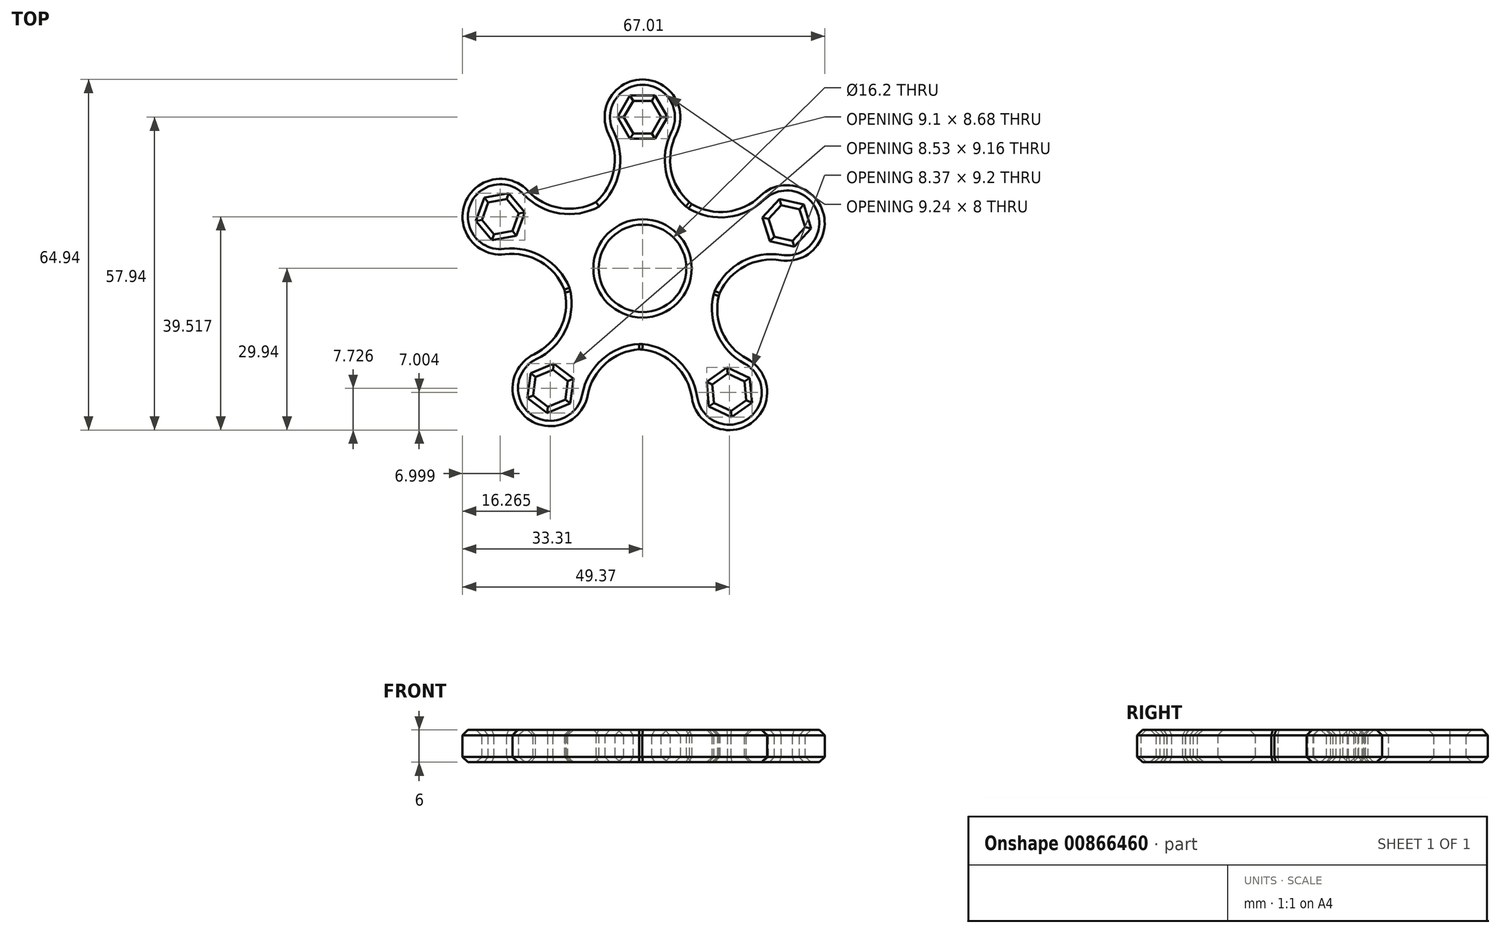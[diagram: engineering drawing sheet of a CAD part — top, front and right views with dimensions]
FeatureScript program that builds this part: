
annotation { "Feature Type Name" : "Feature", "Feature Type Description" : "" }
export const myFeature = defineFeature(function(context is Context, id is Id, definition is map)
    precondition{}
    {
        {
            var Q0;
            Q0=qCreatedBy(makeId("Top.planeOp"),FACE);
            var sketch = newSketch(context, id + "F0", { "sketchPlane" : qUnion([Q0])});
            skCircle(sketch, "E0", {"center": v(0, 0) * mm, "radius": 35 * mm, "construction": true});
            skCircle(sketch, "E1", {"center": v(0, 0) * mm, "radius": 8.1 * mm});
            skCircle(sketch, "E2", {"center": v(0, 0) * mm, "radius": 15 * mm});
            skLineSegment(sketch, "E3", {"start": v(0, 0) * mm, "end": v(0, 35) * mm, "construction": true});
            skLineSegment(sketch, "E4.1.0", {"start": v(0, 0) * mm, "end": v(33.38, 10.52) * mm, "construction": true});
            skLineSegment(sketch, "E4.2.0", {"start": v(0, 0) * mm, "end": v(20.08, -28.67) * mm, "construction": true});
            skLineSegment(sketch, "E4.3.0", {"start": v(0, 0) * mm, "end": v(-21.3, -27.77) * mm, "construction": true});
            skLineSegment(sketch, "E4.4.0", {"start": v(0, 0) * mm, "end": v(-32.89, 11.97) * mm, "construction": true});
            skLineSegment(sketch, "E4.anchor2", {"start": v(0, 0) * mm, "end": v(-32.89, 11.97) * mm, "construction": true});
            skCircle(sketch, "E5", {"center": v(0, 28) * mm, "radius": 7 * mm});
            skArc(sketch, "E6", {"start": v(-8.63, 12.27) * mm, "mid": v(-5.3, 18.15) * mm, "end": v(-6.25, 24.84) * mm});
            skArc(sketch, "E7.MirrorCS", {"start": v(8.63, 12.27) * mm, "mid": v(5.3, 18.15) * mm, "end": v(6.25, 24.84) * mm});
            skArc(sketch, "E8.1.1", {"start": v(14.3, -4.55) * mm, "mid": v(18.9, 0.4) * mm, "end": v(25.57, 1.51) * mm});
            skCircle(sketch, "E8.1.2", {"center": v(26.7, 8.42) * mm, "radius": 7 * mm});
            skArc(sketch, "E8.1.3", {"start": v(9.1, 11.92) * mm, "mid": v(15.71, 10.51) * mm, "end": v(21.81, 13.43) * mm});
            skArc(sketch, "E8.2.1", {"start": v(-0.04, -15) * mm, "mid": v(6.07, -17.9) * mm, "end": v(9.13, -23.93) * mm});
            skCircle(sketch, "E8.2.2", {"center": v(16.06, -22.94) * mm, "radius": 7 * mm});
            skArc(sketch, "E8.2.3", {"start": v(14.1, -5.1) * mm, "mid": v(14.75, -11.82) * mm, "end": v(19.37, -16.77) * mm});
            skArc(sketch, "E8.3.1", {"start": v(-14.32, -4.47) * mm, "mid": v(-15.25, -11.17) * mm, "end": v(-20.08, -15.9) * mm});
            skCircle(sketch, "E8.3.2", {"center": v(-17.05, -22.21) * mm, "radius": 7 * mm});
            skArc(sketch, "E8.3.3", {"start": v(-0.62, -14.99) * mm, "mid": v(-6.84, -17.63) * mm, "end": v(-10.17, -23.51) * mm});
            skArc(sketch, "E8.4.1", {"start": v(-8.57, 12.3) * mm, "mid": v(-15.24, 11.2) * mm, "end": v(-21.2, 14.37) * mm});
            skCircle(sketch, "E8.4.2", {"center": v(-26.31, 9.58) * mm, "radius": 7 * mm});
            skArc(sketch, "E8.4.3", {"start": v(-14.48, -3.92) * mm, "mid": v(-18.87, 1.22) * mm, "end": v(-25.48, 2.63) * mm});
            skLineSegment(sketch, "E8.anchor1", {"start": v(0, 0) * mm, "end": v(-8.63, 12.27) * mm, "construction": true});
            skLineSegment(sketch, "E8.anchor2", {"start": v(0, 0) * mm, "end": v(-14.48, -3.92) * mm, "construction": true});
            skSolve(sketch);
        }
        {
            var Q0;
            Q0 = qSketchRegion(id + "F0", true);
            extrude(context, id + "F1", {"entities" : qUnion([Q0]), "depth" : 6 * mm, "offsetDistance" : 25 * mm});
        }
        {
            var Q0;
            Q0=makeQuery(id+"F1.opExtrude","CAP_FACE",FACE,{"disambiguationData":[OSD([sQuery(id+"F0.wireOp",EDGE,"E1"),sQuery(id+"F0.wireOp",EDGE,"E5"),sQuery(id+"F0.wireOp",EDGE,"E6"),sQuery(id+"F0.wireOp",EDGE,"E7.MirrorCS"),sQuery(id+"F0.wireOp",EDGE,"E8.1.1"),sQuery(id+"F0.wireOp",EDGE,"E8.1.2"),sQuery(id+"F0.wireOp",EDGE,"E8.1.3"),sQuery(id+"F0.wireOp",EDGE,"E8.2.1"),sQuery(id+"F0.wireOp",EDGE,"E8.2.2"),sQuery(id+"F0.wireOp",EDGE,"E8.2.3"),sQuery(id+"F0.wireOp",EDGE,"E8.3.1"),sQuery(id+"F0.wireOp",EDGE,"E8.3.2"),sQuery(id+"F0.wireOp",EDGE,"E8.3.3"),sQuery(id+"F0.wireOp",EDGE,"E2"),sQuery(id+"F0.wireOp",EDGE,"E8.4.1"),sQuery(id+"F0.wireOp",EDGE,"E8.4.2"),sQuery(id+"F0.wireOp",EDGE,"E8.4.3")])],"isStart":false});
            var sketch = newSketch(context, id + "F2", { "sketchPlane" : qUnion([Q0])});
            skCircle(sketch, "E9.cCircle", {"center": v(0, 28) * mm, "radius": 3 * mm, "construction": true});
            skLineSegment(sketch, "E9.0", {"start": v(-1.73, 31) * mm, "end": v(1.73, 31) * mm});
            skLineSegment(sketch, "E9.1", {"start": v(1.73, 31) * mm, "end": v(3.46, 28) * mm});
            skLineSegment(sketch, "E9.2", {"start": v(3.46, 28) * mm, "end": v(1.73, 25) * mm});
            skLineSegment(sketch, "E9.3", {"start": v(1.73, 25) * mm, "end": v(-1.73, 25) * mm});
            skLineSegment(sketch, "E9.4", {"start": v(-1.73, 25) * mm, "end": v(-3.46, 28) * mm});
            skLineSegment(sketch, "E9.5", {"start": v(-3.46, 28) * mm, "end": v(-1.73, 31) * mm});
            skPoint(sketch, "E9.0.midPoint", {"position": v(0, 31) * mm});
            skLineSegment(sketch, "E10.0", {"start": v(0, 0) * mm, "end": v(33.38, 10.52) * mm, "construction": true});
            skLineSegment(sketch, "E11.0", {"start": v(0, 0) * mm, "end": v(20.08, -28.67) * mm, "construction": true});
            skLineSegment(sketch, "E12.0", {"start": v(0, 0) * mm, "end": v(-32.89, 11.97) * mm, "construction": true});
            skLineSegment(sketch, "E13.0", {"start": v(0, 0) * mm, "end": v(-21.3, -27.77) * mm, "construction": true});
            skCircle(sketch, "E14.cCircle", {"center": v(26.7, 8.42) * mm, "radius": 3 * mm, "construction": true});
            skLineSegment(sketch, "E14.0", {"start": v(29.04, 10.97) * mm, "end": v(30.09, 7.67) * mm});
            skLineSegment(sketch, "E14.1", {"start": v(30.09, 7.67) * mm, "end": v(27.75, 5.12) * mm});
            skLineSegment(sketch, "E14.2", {"start": v(27.75, 5.12) * mm, "end": v(24.36, 5.87) * mm});
            skLineSegment(sketch, "E14.3", {"start": v(24.36, 5.87) * mm, "end": v(23.32, 9.17) * mm});
            skLineSegment(sketch, "E14.4", {"start": v(23.32, 9.17) * mm, "end": v(25.66, 11.72) * mm});
            skLineSegment(sketch, "E14.5", {"start": v(25.66, 11.72) * mm, "end": v(29.04, 10.97) * mm});
            skPoint(sketch, "E14.0.midPoint", {"position": v(29.57, 9.32) * mm});
            skCircle(sketch, "E15.cCircle", {"center": v(16.06, -22.94) * mm, "radius": 3 * mm, "construction": true});
            skLineSegment(sketch, "E15.0", {"start": v(19.2, -24.4) * mm, "end": v(16.36, -26.39) * mm});
            skLineSegment(sketch, "E15.1", {"start": v(16.36, -26.39) * mm, "end": v(13.22, -24.92) * mm});
            skLineSegment(sketch, "E15.2", {"start": v(13.22, -24.92) * mm, "end": v(12.92, -21.47) * mm});
            skLineSegment(sketch, "E15.3", {"start": v(12.92, -21.47) * mm, "end": v(15.76, -19.49) * mm});
            skLineSegment(sketch, "E15.4", {"start": v(15.76, -19.49) * mm, "end": v(18.9, -20.95) * mm});
            skLineSegment(sketch, "E15.5", {"start": v(18.9, -20.95) * mm, "end": v(19.2, -24.4) * mm});
            skPoint(sketch, "E15.0.midPoint", {"position": v(17.78, -25.4) * mm});
            skCircle(sketch, "E16.cCircle", {"center": v(-17.05, -22.21) * mm, "radius": 3 * mm, "construction": true});
            skLineSegment(sketch, "E16.0", {"start": v(-16.6, -18.78) * mm, "end": v(-13.84, -20.89) * mm});
            skLineSegment(sketch, "E16.1", {"start": v(-13.84, -20.89) * mm, "end": v(-14.3, -24.32) * mm});
            skLineSegment(sketch, "E16.2", {"start": v(-14.3, -24.32) * mm, "end": v(-17.5, -25.65) * mm});
            skLineSegment(sketch, "E16.3", {"start": v(-17.5, -25.65) * mm, "end": v(-20.25, -23.54) * mm});
            skLineSegment(sketch, "E16.4", {"start": v(-20.25, -23.54) * mm, "end": v(-19.8, -20.1) * mm});
            skLineSegment(sketch, "E16.5", {"start": v(-19.8, -20.1) * mm, "end": v(-16.6, -18.78) * mm});
            skPoint(sketch, "E16.0.midPoint", {"position": v(-15.22, -19.83) * mm});
            skCircle(sketch, "E17.cCircle", {"center": v(-26.31, 9.58) * mm, "radius": 3 * mm, "construction": true});
            skLineSegment(sketch, "E17.0", {"start": v(-22.9, 10.18) * mm, "end": v(-24.08, 6.92) * mm});
            skLineSegment(sketch, "E17.1", {"start": v(-24.08, 6.92) * mm, "end": v(-27.5, 6.32) * mm});
            skLineSegment(sketch, "E17.2", {"start": v(-27.5, 6.32) * mm, "end": v(-29.72, 8.98) * mm});
            skLineSegment(sketch, "E17.3", {"start": v(-29.72, 8.98) * mm, "end": v(-28.54, 12.23) * mm});
            skLineSegment(sketch, "E17.4", {"start": v(-28.54, 12.23) * mm, "end": v(-25.13, 12.83) * mm});
            skLineSegment(sketch, "E17.5", {"start": v(-25.13, 12.83) * mm, "end": v(-22.9, 10.18) * mm});
            skPoint(sketch, "E17.0.midPoint", {"position": v(-23.5, 8.55) * mm});
            skSolve(sketch);
        }
        {
            var Q0;
            Q0 = qSketchRegion(id + "F2", true);
            extrude(context, id + "F3", {"entities" : qUnion([Q0]), "operationType" : NewBodyOperationType.REMOVE, "oppositeDirection" : true, "depth" : 25 * mm, "offsetDistance" : 25 * mm});
        }
        {
            var Q0;
            Q0=makeQuery(id+"F1.opExtrude","CAP_FACE",FACE,{"disambiguationData":[OSD([sQuery(id+"F0.wireOp",EDGE,"E1"),sQuery(id+"F0.wireOp",EDGE,"E5"),sQuery(id+"F0.wireOp",EDGE,"E6"),sQuery(id+"F0.wireOp",EDGE,"E7.MirrorCS"),sQuery(id+"F0.wireOp",EDGE,"E8.1.1"),sQuery(id+"F0.wireOp",EDGE,"E8.1.2"),sQuery(id+"F0.wireOp",EDGE,"E8.1.3"),sQuery(id+"F0.wireOp",EDGE,"E8.2.1"),sQuery(id+"F0.wireOp",EDGE,"E8.2.2"),sQuery(id+"F0.wireOp",EDGE,"E8.2.3"),sQuery(id+"F0.wireOp",EDGE,"E8.3.1"),sQuery(id+"F0.wireOp",EDGE,"E8.3.2"),sQuery(id+"F0.wireOp",EDGE,"E8.3.3"),sQuery(id+"F0.wireOp",EDGE,"E2"),sQuery(id+"F0.wireOp",EDGE,"E8.4.1"),sQuery(id+"F0.wireOp",EDGE,"E8.4.2"),sQuery(id+"F0.wireOp",EDGE,"E8.4.3")])],"isStart":false});
            var Q1;
            Q1=makeQuery(id+"F1.opExtrude","CAP_FACE",FACE,{"disambiguationData":[OSD([sQuery(id+"F0.wireOp",EDGE,"E1"),sQuery(id+"F0.wireOp",EDGE,"E5"),sQuery(id+"F0.wireOp",EDGE,"E6"),sQuery(id+"F0.wireOp",EDGE,"E7.MirrorCS"),sQuery(id+"F0.wireOp",EDGE,"E8.1.1"),sQuery(id+"F0.wireOp",EDGE,"E8.1.2"),sQuery(id+"F0.wireOp",EDGE,"E8.1.3"),sQuery(id+"F0.wireOp",EDGE,"E8.2.1"),sQuery(id+"F0.wireOp",EDGE,"E8.2.2"),sQuery(id+"F0.wireOp",EDGE,"E8.2.3"),sQuery(id+"F0.wireOp",EDGE,"E8.3.1"),sQuery(id+"F0.wireOp",EDGE,"E8.3.2"),sQuery(id+"F0.wireOp",EDGE,"E8.3.3"),sQuery(id+"F0.wireOp",EDGE,"E2"),sQuery(id+"F0.wireOp",EDGE,"E8.4.1"),sQuery(id+"F0.wireOp",EDGE,"E8.4.2"),sQuery(id+"F0.wireOp",EDGE,"E8.4.3")])],"isStart":true});
            chamfer(context, id + "F4", {"entities" : qUnion([Q0, Q1]), "width" : 1 * mm, "tangentPropagation" : true});
        }
    });
